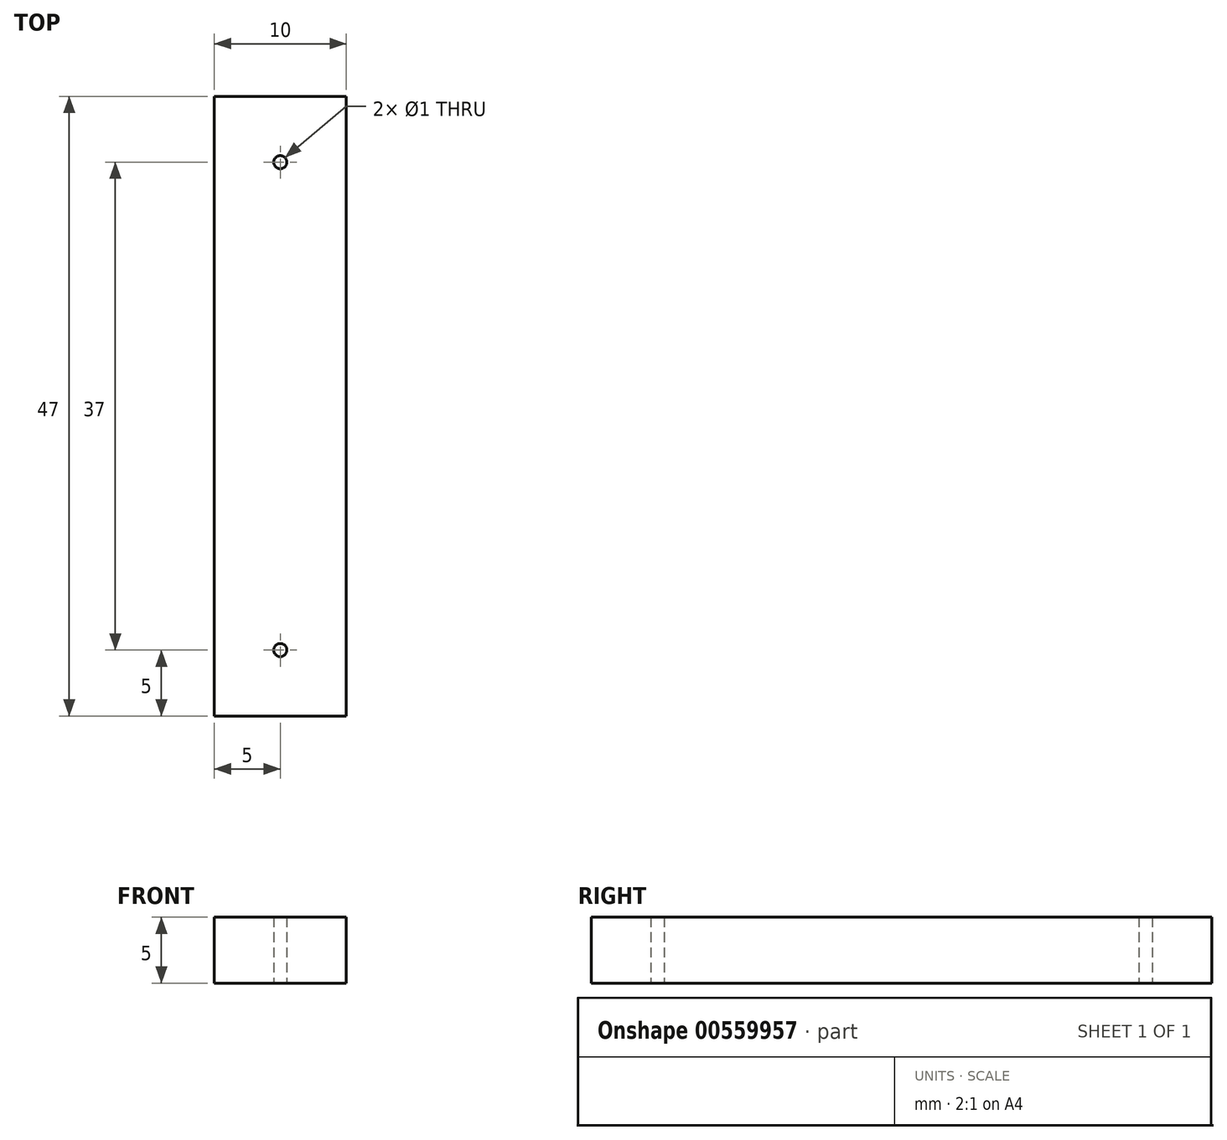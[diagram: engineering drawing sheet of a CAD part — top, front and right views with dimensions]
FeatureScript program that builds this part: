
annotation { "Feature Type Name" : "Feature", "Feature Type Description" : "" }
export const myFeature = defineFeature(function(context is Context, id is Id, definition is map)
    precondition{}
    {
        {
            var Q0;
            Q0=qCreatedBy(makeId("Top.planeOp"),FACE);
            var sketch = newSketch(context, id + "F0", { "sketchPlane" : qUnion([Q0])});
            skLineSegment(sketch, "E0.bottom", {"start": v(0, 0) * mm, "end": v(10, 0) * mm});
            skLineSegment(sketch, "E0.top", {"start": v(0, 47) * mm, "end": v(10, 47) * mm});
            skLineSegment(sketch, "E0.left", {"start": v(0, 0) * mm, "end": v(0, 47) * mm});
            skLineSegment(sketch, "E0.right", {"start": v(10, 0) * mm, "end": v(10, 47) * mm});
            skCircle(sketch, "E1", {"center": v(5, 42) * mm, "radius": 0.5 * mm});
            skCircle(sketch, "E2", {"center": v(5, 5) * mm, "radius": 0.5 * mm});
            skSolve(sketch);
        }
        {
            var Q0;
            Q0=makeQuery(id+"F0.imprint","IMPRINT",FACE,{"disambiguationData":[TD([[makeQuery(id+"F0.imprint","IMPRINT",EDGE,{"derivedFrom":sQuery(id+"F0.wireOp",EDGE,"E0.bottom")}),1.0]])]});
            extrude(context, id + "F1", {"entities" : qUnion([Q0]), "depth" : 5 * mm, "offsetDistance" : 25 * mm});
        }
    });
